# Revit family: Faucet-Single-American_Standard-Serin-2064.15X_Series
name_source: partatom
category: Plumbing Fixtures
revit_build: Autodesk Revit 2014 (Build: 20130308_1515(x64)
units: mm (PartAtom-declared; Revit-internal decimal feet)

## types (2) — shared parameters
ADA Compliant = Yes
Assembly Code = D2020300
CW Connection = Yes
CWFU = 1.5
Connection Diameter = 3/8"
Default Elevation = 0"
Finish = Brass-American Standard-002-Polished Chrome
Flow Rate = 1 GPM
HW Connection = Yes
HWFU = 1.5
Height = 12 5/8"
Installation Type = Deck Mounted
Length = 6 7/8"
Manufacturer = American Standard
Material = Brass-American Standard-002-Polished Chrome
Price = Prices may vary. Please consult Manufacturer Representative for most up-to-date price list.
Product Documentation Link = https://www.americanstandard-us.com
Product Page URL = https://www.americanstandard-us.com
Revised Date = 12/06/2017
Specification = Single control lavatory faucet shall feature a brass body and metal lever handle. Fitting shall be equipped with flexible supplies with 3/8in compression connectors. Shall also feature washerless ceramic disc valve cartridge with an integral hot limit safety stop.
URL = http://www.americanstandard-us.com
Vent Connection = No
WFU = 2
Warranty Information = Limited Lifetime Function and Finish Warranty
Waste Connection = No
Width = 1 7/8"

## per-type parameters (varying)
| type | Description |
| 2064.152 | Serin Single Control Vessel Faucet. Grid Drain. |
| 2064.151 | Serin Single Control Vessel Faucet. Less Drain. |

note: column(s) folded — value = type name in every type: Model

## geometry (parser evidence)
native form markers: Sweep x1
no freeform markers — native parametric forms only
